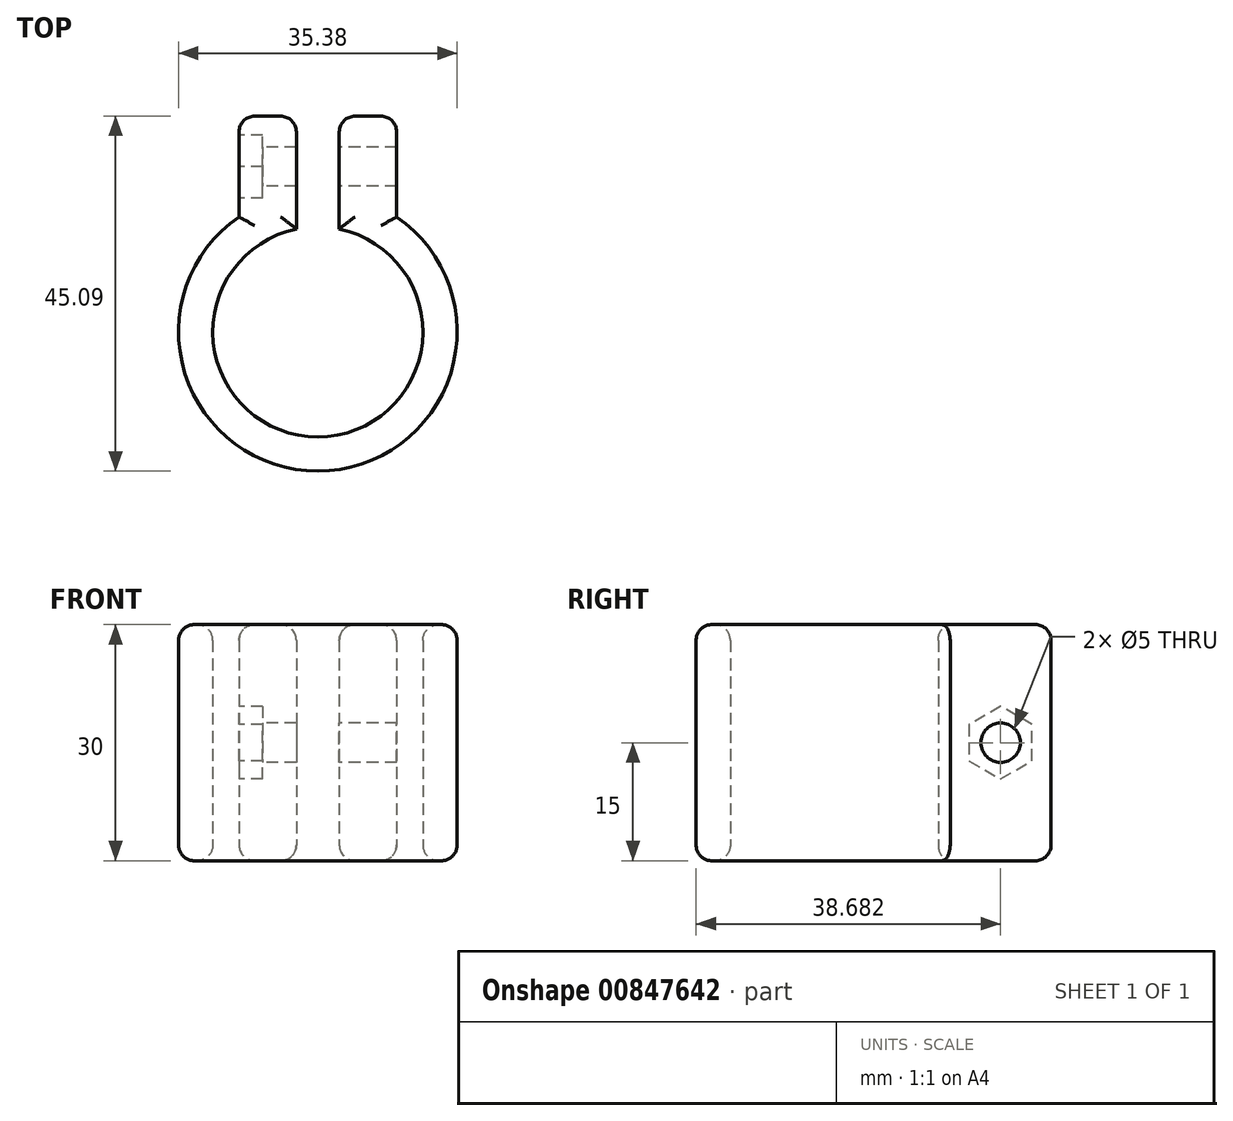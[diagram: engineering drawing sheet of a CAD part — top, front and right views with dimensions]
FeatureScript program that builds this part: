
annotation { "Feature Type Name" : "Feature", "Feature Type Description" : "" }
export const myFeature = defineFeature(function(context is Context, id is Id, definition is map)
    precondition{}
    {
        {
            var Q0;
            Q0=qCreatedBy(makeId("Top.planeOp"),FACE);
            var sketch = newSketch(context, id + "F0", { "sketchPlane" : qUnion([Q0])});
            skArc(sketch, "E0", {"start": v(-2.73, 13.07) * mm, "mid": v(0, -13.35) * mm, "end": v(2.73, 13.07) * mm});
            skArc(sketch, "E1", {"start": v(-2.73, 17.48) * mm, "mid": v(0, -17.69) * mm, "end": v(2.73, 17.48) * mm});
            skLineSegment(sketch, "E2.left", {"start": v(-2.73, 17.48) * mm, "end": v(-2.73, 13.07) * mm});
            skLineSegment(sketch, "E2.right", {"start": v(2.73, 17.48) * mm, "end": v(2.73, 13.07) * mm});
            skPoint(sketch, "E3.orphan", {"position": v(-2.73, 20.43) * mm});
            skPoint(sketch, "E4.orphan", {"position": v(2.73, 20.43) * mm});
            skLineSegment(sketch, "E5.bottom", {"start": v(10, 27.4) * mm, "end": v(2.73, 27.4) * mm});
            skLineSegment(sketch, "E5.left", {"start": v(10, 27.4) * mm, "end": v(10, 14.59) * mm});
            skLineSegment(sketch, "E5.right", {"start": v(-10, 27.4) * mm, "end": v(-10, 14.59) * mm});
            skPoint(sketch, "E6.trimOffspring.end.orphan", {"position": v(2.73, -20.43) * mm});
            skPoint(sketch, "E7.trimOffspring.end.orphan", {"position": v(-2.73, -20.43) * mm});
            skPoint(sketch, "E5.top.end.orphan", {"position": v(-10, -27.4) * mm});
            skPoint(sketch, "E5.top.start.orphan", {"position": v(10, -27.4) * mm});
            skLineSegment(sketch, "E8", {"start": v(-2.73, 13.07) * mm, "end": v(-2.73, 27.4) * mm});
            skLineSegment(sketch, "E9", {"start": v(2.73, 13.07) * mm, "end": v(2.73, 27.4) * mm});
            skLineSegment(sketch, "E10.trimOffspring", {"start": v(-2.73, 27.4) * mm, "end": v(-10, 27.4) * mm});
            skSolve(sketch);
        }
        {
            var Q0;
            Q0=makeQuery(id+"F0.imprint","IMPRINT",FACE,{"disambiguationData":[TD([[makeQuery(id+"F0.imprint","IMPRINT",EDGE,{"derivedFrom":sQuery(id+"F0.wireOp",EDGE,"E0")}),-1.0]])]});
            var Q1;
            {var subQ2=sQuery(id+"F0.wireOp",EDGE,"E5.right");Q1=makeQuery(id+"F0.imprint","IMPRINT",FACE,{"disambiguationData":[TD([[makeQuery(id+"F0.imprint","IMPRINT",EDGE,{"derivedFrom":subQ2}),1.0]])]});}
            var Q2;
            Q2=makeQuery(id+"F0.imprint","IMPRINT",FACE,{"disambiguationData":[TD([[makeQuery(id+"F0.imprint","IMPRINT",EDGE,{"derivedFrom":sQuery(id+"F0.wireOp",EDGE,"E5.bottom")}),1.0]])]});
            extrude(context, id + "F1", {"entities" : qUnion([Q0, Q1, Q2]), "depth" : 30 * mm, "offsetDistance" : 25 * mm});
        }
        {
            var Q0;
            Q0=makeQuery(id+"F1.opExtrude","SWEPT_FACE",FACE,{"disambiguationData":[OSD([sQuery(id+"F0.wireOp",EDGE,"E5.right")])]});
            var sketch = newSketch(context, id + "F2", { "sketchPlane" : qUnion([Q0])});
            skCircle(sketch, "E11", {"center": v(-21, 15) * mm, "radius": 2.5 * mm});
            skPoint(sketch, "E11.centerSnap0", {"position": v(-21, 30) * mm});
            skPoint(sketch, "E11.centerSnap1", {"position": v(-14.59, 15) * mm});
            skSolve(sketch);
        }
        {
            var Q0;
            Q0=makeQuery(id+"F2.imprint","IMPRINT",FACE,{"disambiguationData":[TD([[makeQuery(id+"F2.imprint","IMPRINT",EDGE,{"derivedFrom":sQuery(id+"F2.wireOp",EDGE,"E11")}),1.0]])]});
            extrude(context, id + "F3", {"entities" : qUnion([Q0]), "operationType" : NewBodyOperationType.REMOVE, "endBound" : BoundingType.THROUGH_ALL, "oppositeDirection" : true, "depth" : 25 * mm, "offsetDistance" : 25 * mm});
        }
        {
            var Q0;
            Q0=makeQuery(id+"F1.opExtrude","SWEPT_FACE",FACE,{"disambiguationData":[OSD([sQuery(id+"F0.wireOp",EDGE,"E5.right")])]});
            var sketch = newSketch(context, id + "F4", { "sketchPlane" : qUnion([Q0])});
            skLineSegment(sketch, "E12", {"start": v(-21, 30) * mm, "end": v(-21, 0) * mm, "construction": true});
            skLineSegment(sketch, "E13", {"start": v(-27.4, 15) * mm, "end": v(-14.59, 15) * mm, "construction": true});
            skCircle(sketch, "E14.cCircle", {"center": v(-21, 15) * mm, "radius": 4 * mm, "construction": true});
            skLineSegment(sketch, "E14.0", {"start": v(-25, 12.7) * mm, "end": v(-25, 17.3) * mm});
            skLineSegment(sketch, "E14.1", {"start": v(-25, 17.3) * mm, "end": v(-21, 19.62) * mm});
            skLineSegment(sketch, "E14.2", {"start": v(-21, 19.62) * mm, "end": v(-17, 17.3) * mm});
            skLineSegment(sketch, "E14.3", {"start": v(-17, 17.3) * mm, "end": v(-17, 12.7) * mm});
            skLineSegment(sketch, "E14.4", {"start": v(-17, 12.7) * mm, "end": v(-21, 10.38) * mm});
            skLineSegment(sketch, "E14.5", {"start": v(-21, 10.38) * mm, "end": v(-25, 12.7) * mm});
            skPoint(sketch, "E14.0.midPoint", {"position": v(-25, 15) * mm});
            skSolve(sketch);
        }
        {
            var Q0;
            Q0=makeQuery(id+"F4.imprint","IMPRINT",FACE,{"disambiguationData":[TD([[makeQuery(id+"F4.imprint","IMPRINT",EDGE,{"derivedFrom":sQuery(id+"F4.wireOp",EDGE,"E14.0")}),-1.0]])]});
            extrude(context, id + "F5", {"entities" : qUnion([Q0]), "operationType" : NewBodyOperationType.REMOVE, "oppositeDirection" : true, "depth" : 3 * mm, "offsetDistance" : 25 * mm});
        }
        {
            var Q0;
            Q0=makeQuery(id+"F1.opExtrude","CAP_FACE",FACE,{"disambiguationData":[OSD([sQuery(id+"F0.wireOp",EDGE,"E0"),sQuery(id+"F0.wireOp",EDGE,"E1"),sQuery(id+"F0.wireOp",EDGE,"E2.left"),sQuery(id+"F0.wireOp",EDGE,"E2.right"),sQuery(id+"F0.wireOp",EDGE,"E5.bottom"),sQuery(id+"F0.wireOp",EDGE,"E5.left"),sQuery(id+"F0.wireOp",EDGE,"E5.right"),sQuery(id+"F0.wireOp",EDGE,"E8"),sQuery(id+"F0.wireOp",EDGE,"E9"),sQuery(id+"F0.wireOp",EDGE,"E10.trimOffspring")])],"isStart":false});
            var Q1;
            Q1=makeQuery(id+"F1.opExtrude","CAP_FACE",FACE,{"disambiguationData":[OSD([sQuery(id+"F0.wireOp",EDGE,"E0"),sQuery(id+"F0.wireOp",EDGE,"E1"),sQuery(id+"F0.wireOp",EDGE,"E2.left"),sQuery(id+"F0.wireOp",EDGE,"E2.right"),sQuery(id+"F0.wireOp",EDGE,"E5.bottom"),sQuery(id+"F0.wireOp",EDGE,"E5.left"),sQuery(id+"F0.wireOp",EDGE,"E5.right"),sQuery(id+"F0.wireOp",EDGE,"E8"),sQuery(id+"F0.wireOp",EDGE,"E9"),sQuery(id+"F0.wireOp",EDGE,"E10.trimOffspring")])],"isStart":true});
            var Q2;
            Q2=makeQuery(id+"F1.opExtrude","SWEPT_FACE",FACE,{"disambiguationData":[OSD([sQuery(id+"F0.wireOp",EDGE,"E5.bottom")])]});
            var Q3;
            Q3=makeQuery(id+"F1.opExtrude","SWEPT_FACE",FACE,{"disambiguationData":[OSD([sQuery(id+"F0.wireOp",EDGE,"E10.trimOffspring")])]});
            fillet(context, id + "F6", {"entities" : qUnion([Q0, Q1, Q2, Q3]), "radius" : 2 * mm, "tangentPropagation" : true, "allowEdgeOverflow" : false});
        }
    });
